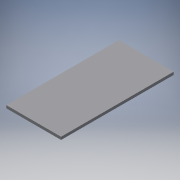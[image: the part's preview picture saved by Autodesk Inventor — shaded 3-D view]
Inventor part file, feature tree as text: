
AUTODESK INVENTOR PART (.ipt)
format: ipt  version: 2016 (Build 200138000, 138)  size: 86,528 bytes
history: native  units: mm
features: other x1, extrude x1, sketch x1, reference x1
ambient origin geometry x8: Origin, YZ Plane, XZ Plane, XY Plane, X Axis, Y Axis, Z Axis, Center Point
bodies: Body1 (feature_tree)
feature tree (4):
  other  "ソリッド1"
  extrude  "押し出し1"  Depth=14.5mm
  sketch  "スケッチ1"
  reference  "参照1"
